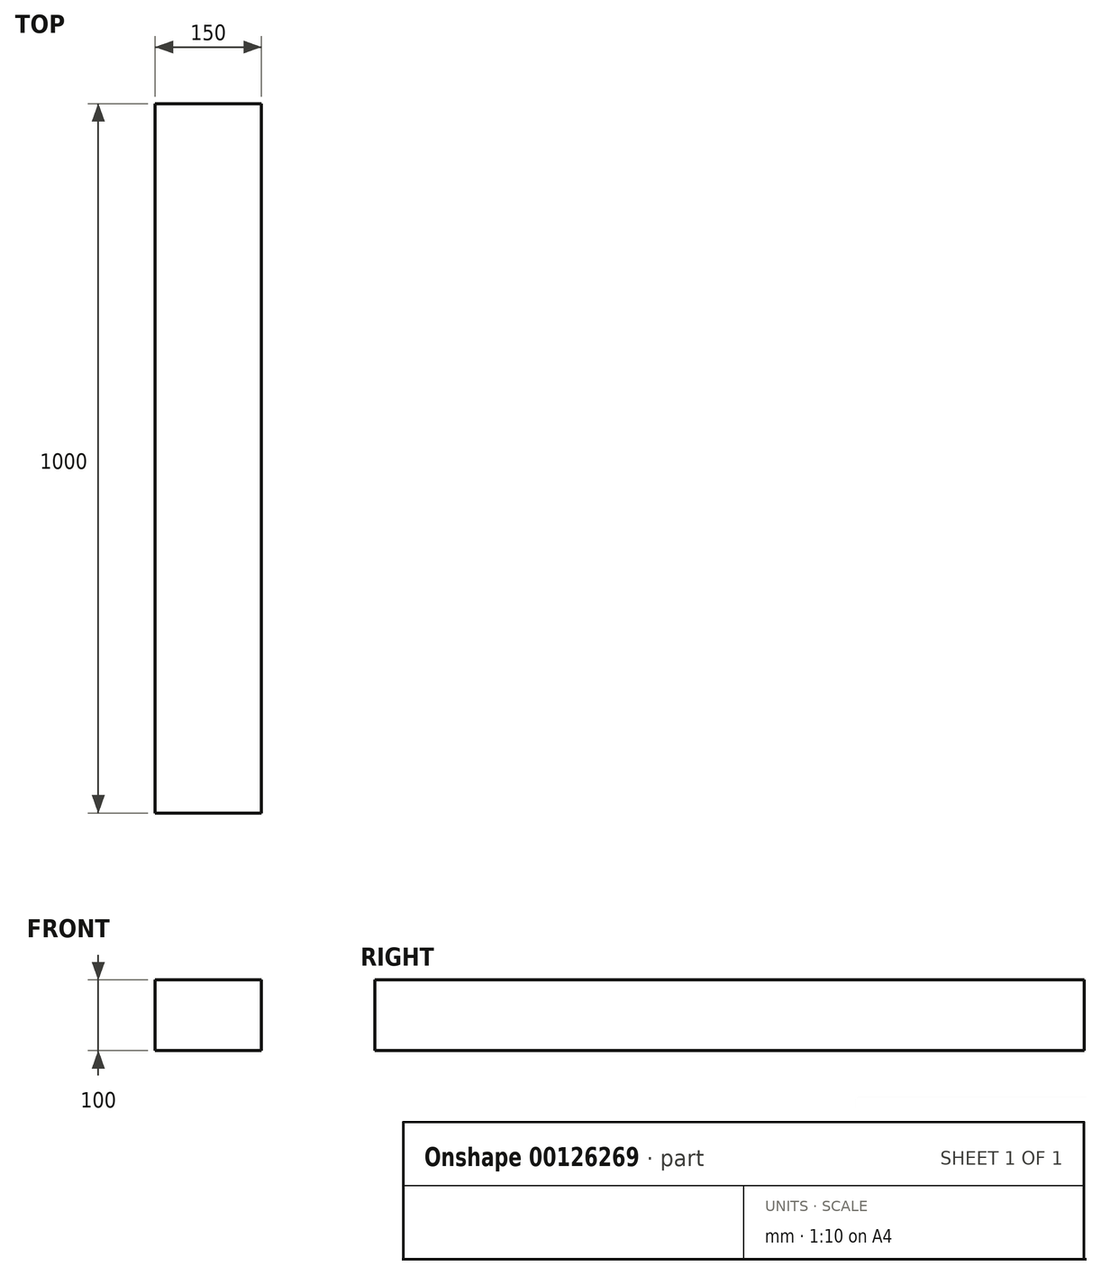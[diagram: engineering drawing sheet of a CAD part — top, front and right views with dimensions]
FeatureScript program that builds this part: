
annotation { "Feature Type Name" : "Feature", "Feature Type Description" : "" }
export const myFeature = defineFeature(function(context is Context, id is Id, definition is map)
    precondition{}
    {
        {
            var Q0;
            Q0=qCreatedBy(makeId("Front.planeOp"),FACE);
            var sketch = newSketch(context, id + "F0", { "sketchPlane" : qUnion([Q0])});
            skLineSegment(sketch, "E0", {"start": v(-712.5, 0) * mm, "end": v(706.25, 0) * mm, "construction": true});
            skLineSegment(sketch, "E1", {"start": v(0, -559.37) * mm, "end": v(0, 528.12) * mm, "construction": true});
            skLineSegment(sketch, "E2", {"start": v(-75, -50) * mm, "end": v(75, -50) * mm});
            skLineSegment(sketch, "E3", {"start": v(75, -50) * mm, "end": v(75, 50) * mm});
            skLineSegment(sketch, "E4", {"start": v(75, 50) * mm, "end": v(-75, 50) * mm});
            skLineSegment(sketch, "E5", {"start": v(-75, 50) * mm, "end": v(-75, -50) * mm});
            skSolve(sketch);
        }
        {
            var Q0;
            Q0 = qSketchRegion(id + "F0", true);
            extrude(context, id + "F1", {"entities" : qUnion([Q0]), "oppositeDirection" : true, "depth" : 1000 * mm});
        }
    });
